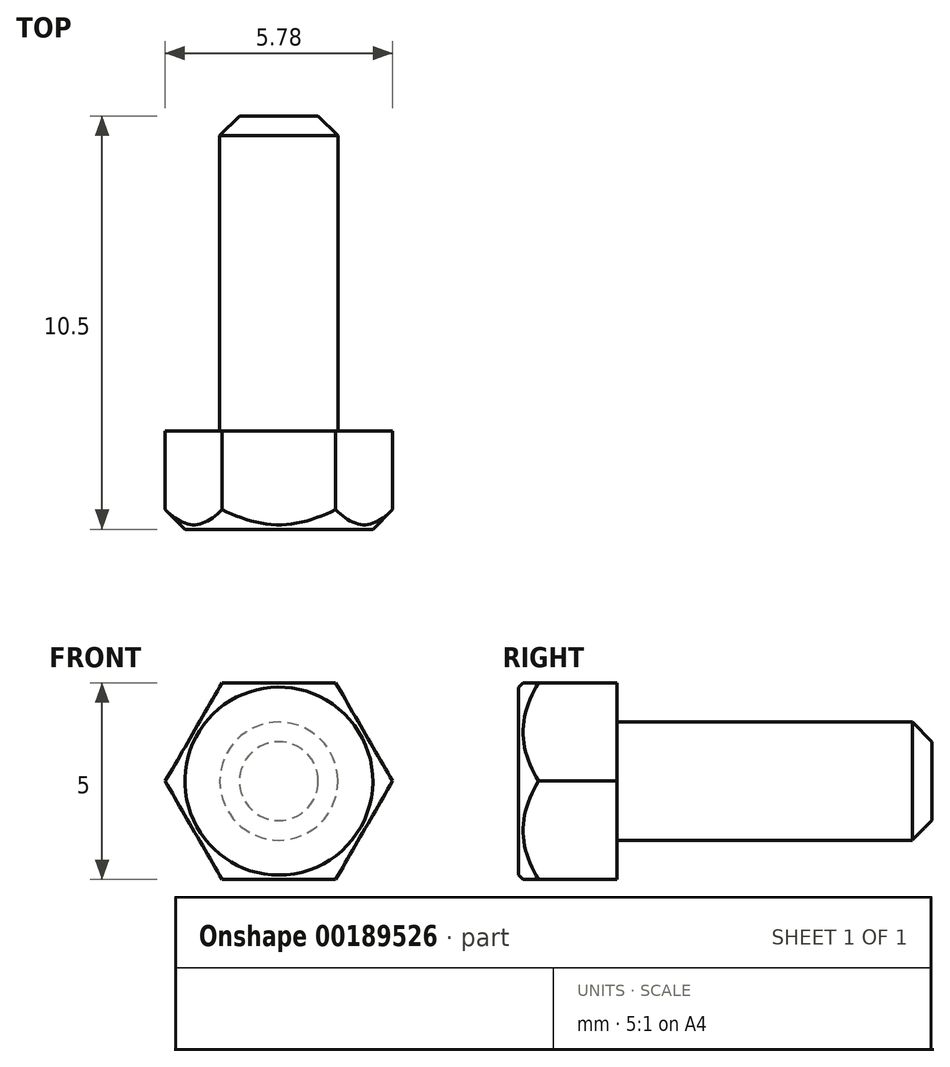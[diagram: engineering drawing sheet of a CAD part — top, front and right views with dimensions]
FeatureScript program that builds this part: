
annotation { "Feature Type Name" : "Feature", "Feature Type Description" : "" }
export const myFeature = defineFeature(function(context is Context, id is Id, definition is map)
    precondition{}
    {
        {
            var Q0;
            Q0=qCreatedBy(makeId("Front.planeOp"),FACE);
            var sketch = newSketch(context, id + "F0", { "sketchPlane" : qUnion([Q0])});
            skCircle(sketch, "E0.cCircle", {"center": v(0, 0) * mm, "radius": 2.5 * mm, "construction": true});
            skLineSegment(sketch, "E0.0", {"start": v(-1.44, 2.5) * mm, "end": v(1.44, 2.5) * mm});
            skLineSegment(sketch, "E0.1", {"start": v(1.44, 2.5) * mm, "end": v(2.89, 0) * mm});
            skLineSegment(sketch, "E0.2", {"start": v(2.89, 0) * mm, "end": v(1.44, -2.5) * mm});
            skLineSegment(sketch, "E0.3", {"start": v(1.44, -2.5) * mm, "end": v(-1.44, -2.5) * mm});
            skLineSegment(sketch, "E0.4", {"start": v(-1.44, -2.5) * mm, "end": v(-2.89, 0) * mm});
            skLineSegment(sketch, "E0.5", {"start": v(-2.89, 0) * mm, "end": v(-1.44, 2.5) * mm});
            skPoint(sketch, "E0.0.midPoint", {"position": v(0, 2.5) * mm});
            skCircle(sketch, "E1", {"center": v(0, 0) * mm, "radius": 1.5 * mm});
            skCircle(sketch, "E2", {"center": v(0, 0) * mm, "radius": 2.89 * mm});
            skSolve(sketch);
        }
        {
            var Q0;
            Q0=makeQuery(id+"F0.imprint","IMPRINT",FACE,{"disambiguationData":[TD([[makeQuery(id+"F0.imprint","IMPRINT",EDGE,{"derivedFrom":sQuery(id+"F0.wireOp",EDGE,"E1")}),1.0]])]});
            var Q1;
            Q1=makeQuery(id+"F0.imprint","IMPRINT",FACE,{"disambiguationData":[TD([[makeQuery(id+"F0.imprint","IMPRINT",EDGE,{"derivedFrom":sQuery(id+"F0.wireOp",EDGE,"E0.0")}),-1.0]])]});
            var Q2;
            {var subQ0=sQuery(id+"F0.wireOp",EDGE,"E0.1");Q2=makeQuery(id+"F0.imprint","IMPRINT",FACE,{"disambiguationData":[TD([[makeQuery(id+"F0.imprint","IMPRINT",EDGE,{"derivedFrom":subQ0}),1.0]])]});}
            var Q3;
            {var subQ0=sQuery(id+"F0.wireOp",EDGE,"E0.0");Q3=makeQuery(id+"F0.imprint","IMPRINT",FACE,{"disambiguationData":[TD([[makeQuery(id+"F0.imprint","IMPRINT",EDGE,{"derivedFrom":subQ0}),1.0]])]});}
            var Q4;
            {var subQ0=sQuery(id+"F0.wireOp",EDGE,"E0.3");Q4=makeQuery(id+"F0.imprint","IMPRINT",FACE,{"disambiguationData":[TD([[makeQuery(id+"F0.imprint","IMPRINT",EDGE,{"derivedFrom":subQ0}),1.0]])]});}
            var Q5;
            {var subQ0=sQuery(id+"F0.wireOp",EDGE,"E0.2");Q5=makeQuery(id+"F0.imprint","IMPRINT",FACE,{"disambiguationData":[TD([[makeQuery(id+"F0.imprint","IMPRINT",EDGE,{"derivedFrom":subQ0}),1.0]])]});}
            var Q6;
            {var subQ0=sQuery(id+"F0.wireOp",EDGE,"E0.4");Q6=makeQuery(id+"F0.imprint","IMPRINT",FACE,{"disambiguationData":[TD([[makeQuery(id+"F0.imprint","IMPRINT",EDGE,{"derivedFrom":subQ0}),1.0]])]});}
            var Q7;
            {var subQ0=sQuery(id+"F0.wireOp",EDGE,"E0.5");Q7=makeQuery(id+"F0.imprint","IMPRINT",FACE,{"disambiguationData":[TD([[makeQuery(id+"F0.imprint","IMPRINT",EDGE,{"derivedFrom":subQ0}),1.0]])]});}
            extrude(context, id + "F1", {"entities" : qUnion([Q0, Q1, Q2, Q3, Q4, Q5, Q6, Q7]), "depth" : 2.5 * mm});
        }
        {
            var Q0;
            Q0=makeQuery(id+"F1.opExtrude","CAP_FACE",FACE,{"disambiguationData":[OSD([sQuery(id+"F0.wireOp",EDGE,"E2")])],"isStart":false});
            chamfer(context, id + "F2", {"entities" : qUnion([Q0]), "width" : 0.5 * mm, "tangentPropagation" : true});
        }
        {
            var Q0;
            Q0=makeQuery(id+"F0.imprint","IMPRINT",FACE,{"disambiguationData":[TD([[makeQuery(id+"F0.imprint","IMPRINT",EDGE,{"derivedFrom":sQuery(id+"F0.wireOp",EDGE,"E0.0")}),-1.0]])]});
            var Q1;
            Q1=makeQuery(id+"F0.imprint","IMPRINT",FACE,{"disambiguationData":[TD([[makeQuery(id+"F0.imprint","IMPRINT",EDGE,{"derivedFrom":sQuery(id+"F0.wireOp",EDGE,"E1")}),1.0]])]});
            extrude(context, id + "F3", {"entities" : qUnion([Q0, Q1]), "operationType" : NewBodyOperationType.INTERSECT, "depth" : 25 * mm});
        }
        {
            var Q0;
            Q0=makeQuery(id+"F0.imprint","IMPRINT",FACE,{"disambiguationData":[TD([[makeQuery(id+"F0.imprint","IMPRINT",EDGE,{"derivedFrom":sQuery(id+"F0.wireOp",EDGE,"E1")}),1.0]])]});
            extrude(context, id + "F4", {"entities" : qUnion([Q0]), "operationType" : NewBodyOperationType.ADD, "oppositeDirection" : true, "depth" : 8 * mm});
        }
        {
            var Q0;
            Q0=makeQuery(id+"F4.opExtrude","CAP_EDGE",EDGE,{"disambiguationData":[OSD([sQuery(id+"F0.wireOp",EDGE,"E1")])],"isStart":false});
            chamfer(context, id + "F5", {"entities" : qUnion([Q0]), "width" : 0.5 * mm, "tangentPropagation" : true});
        }
    });
